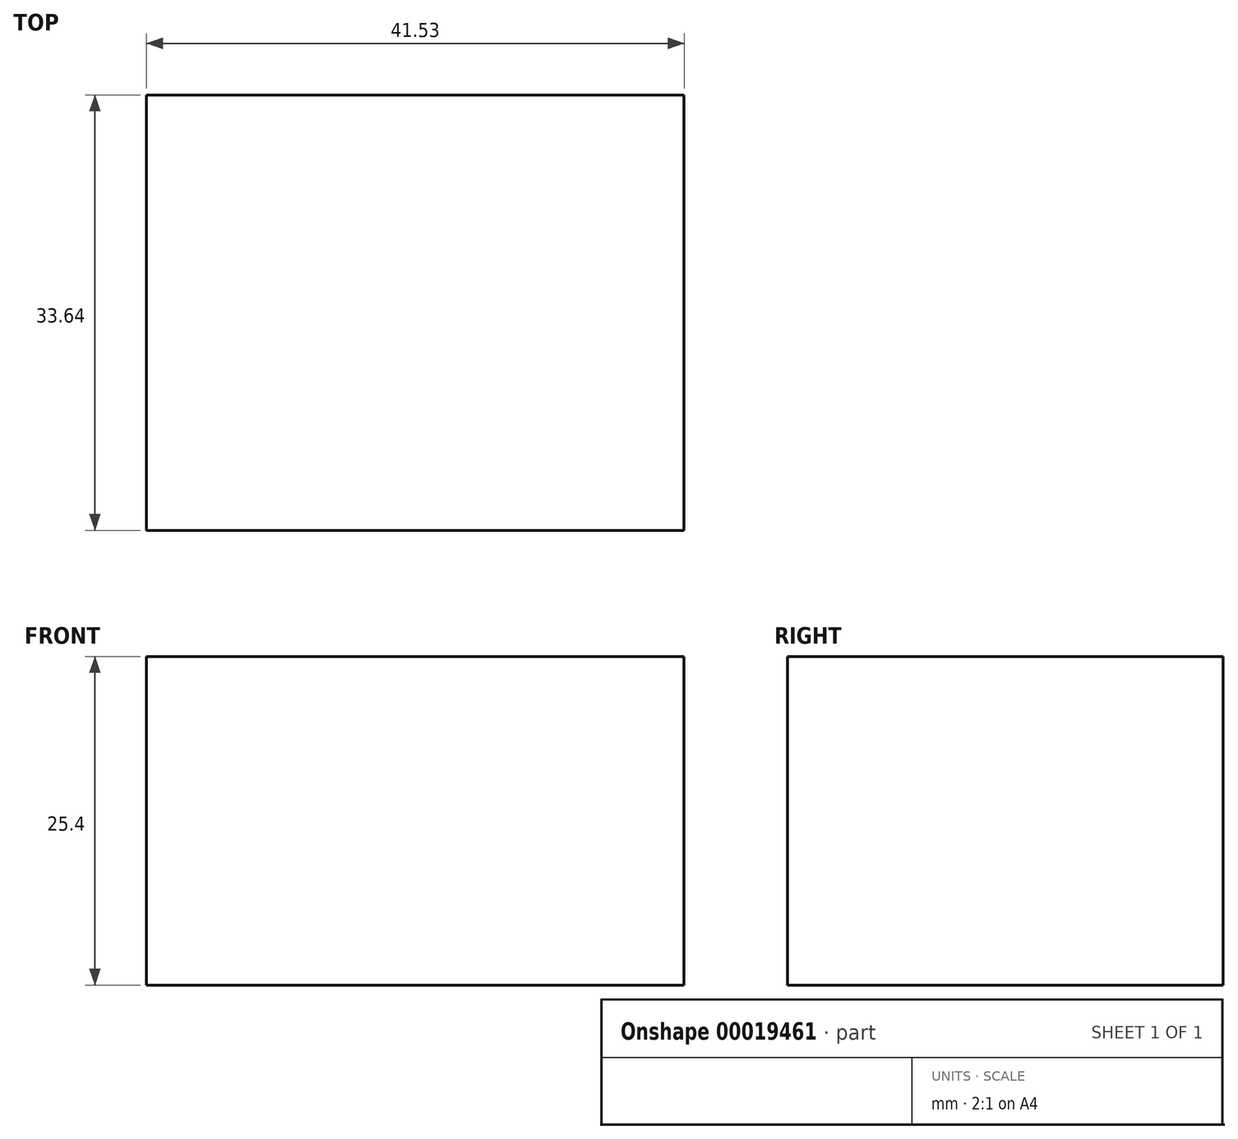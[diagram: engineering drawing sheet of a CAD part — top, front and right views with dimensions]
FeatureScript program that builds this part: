
annotation { "Feature Type Name" : "Feature", "Feature Type Description" : "" }
export const myFeature = defineFeature(function(context is Context, id is Id, definition is map)
    precondition{}
    {
        {
            var Q0;
            Q0=qCreatedBy(makeId("Top.planeOp"),FACE);
            var sketch = newSketch(context, id + "F0", { "sketchPlane" : qUnion([Q0])});
            skLineSegment(sketch, "E0.bottom", {"start": v(0, 0) * mm, "end": v(41.53, 0) * mm});
            skLineSegment(sketch, "E0.top", {"start": v(0, 33.64) * mm, "end": v(41.53, 33.64) * mm});
            skLineSegment(sketch, "E0.left", {"start": v(0, 0) * mm, "end": v(0, 33.64) * mm});
            skLineSegment(sketch, "E0.right", {"start": v(41.53, 0) * mm, "end": v(41.53, 33.64) * mm});
            skSolve(sketch);
        }
        {
            var Q0;
            Q0 = qSketchRegion(id + "F0", true);
            extrude(context, id + "F1", {"entities" : qUnion([Q0]), "depth" : 25.4 * mm});
        }
    });
